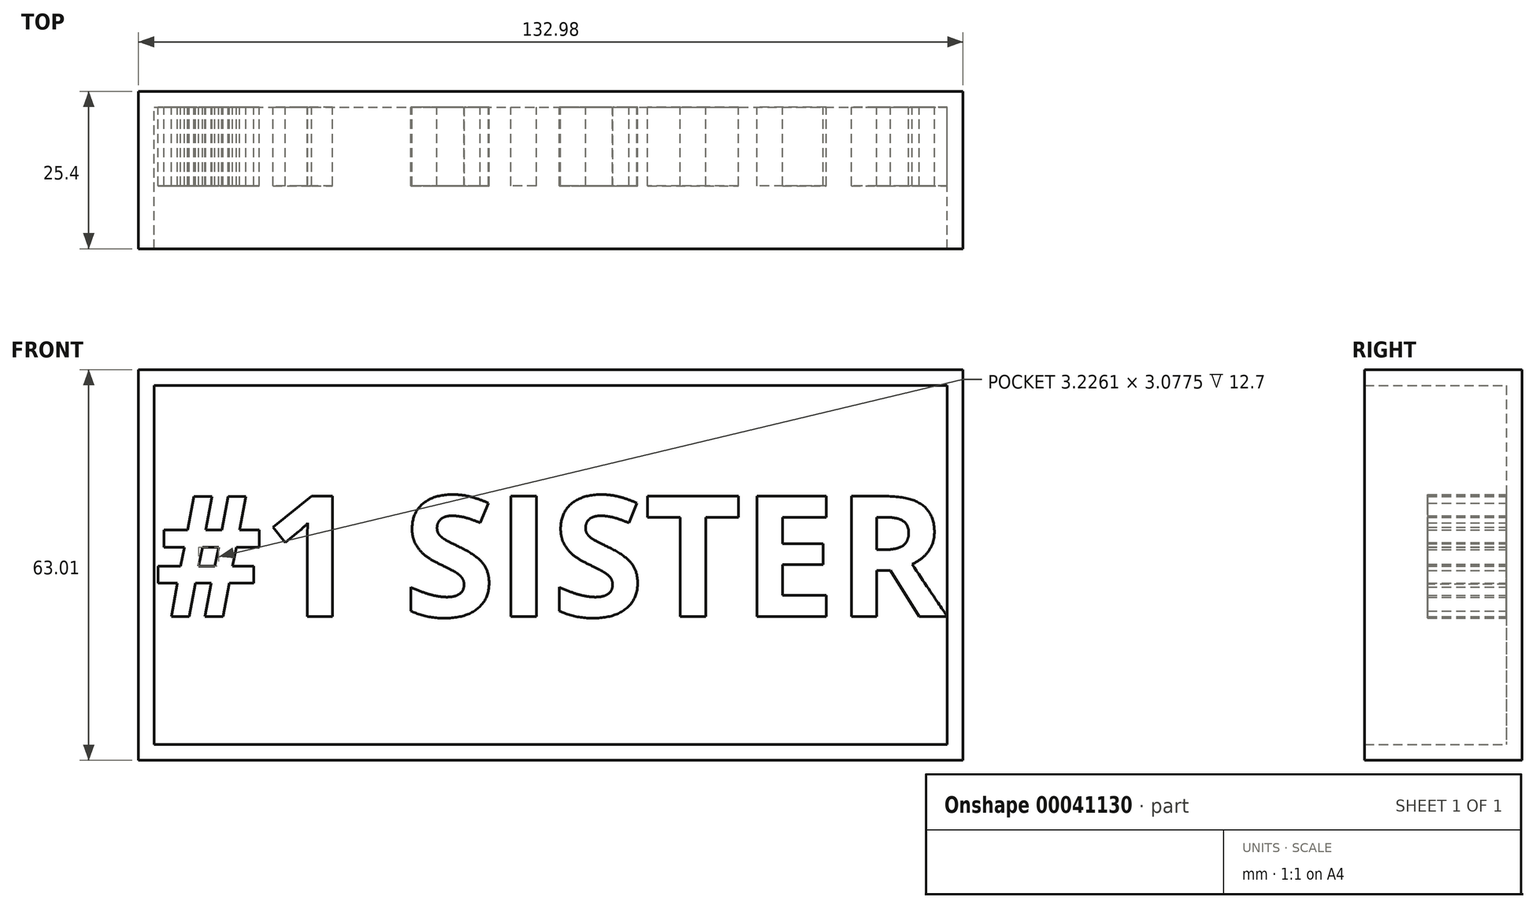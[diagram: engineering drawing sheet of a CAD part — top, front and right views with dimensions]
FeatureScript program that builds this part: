
annotation { "Feature Type Name" : "Feature", "Feature Type Description" : "" }
export const myFeature = defineFeature(function(context is Context, id is Id, definition is map)
    precondition{}
    {
        {
            var Q0;
            Q0=qCreatedBy(makeId("Front.planeOp"),FACE);
            var sketch = newSketch(context, id + "F0", { "sketchPlane" : qUnion([Q0])});
            skLineSegment(sketch, "E0.bottom", {"start": v(-75.97, 55.76) * mm, "end": v(57.01, 55.76) * mm});
            skLineSegment(sketch, "E0.top", {"start": v(-75.97, -7.25) * mm, "end": v(57.01, -7.25) * mm});
            skLineSegment(sketch, "E0.left", {"start": v(-75.97, 55.76) * mm, "end": v(-75.97, -7.25) * mm});
            skLineSegment(sketch, "E0.right", {"start": v(57.01, 55.76) * mm, "end": v(57.01, -7.25) * mm});
            skSolve(sketch);
        }
        {
            var Q0;
            Q0=makeQuery(id+"F0.imprint","IMPRINT",FACE,{"disambiguationData":[TD([[makeQuery(id+"F0.imprint","IMPRINT",EDGE,{"derivedFrom":sQuery(id+"F0.wireOp",EDGE,"E0.bottom")}),-1.0]])]});
            extrude(context, id + "F1", {"entities" : qUnion([Q0]), "depth" : 25.4 * mm});
        }
        {
            var Q0;
            Q0=makeQuery(id+"F1.opExtrude","CAP_FACE",FACE,{"disambiguationData":[OSD([sQuery(id+"F0.wireOp",EDGE,"E0.bottom"),sQuery(id+"F0.wireOp",EDGE,"E0.top"),sQuery(id+"F0.wireOp",EDGE,"E0.left"),sQuery(id+"F0.wireOp",EDGE,"E0.right")])],"isStart":false});
            shell(context, id + "F2", {"entities" : qUnion([Q0]), "thickness" : 2.54 * mm});
        }
        {
            var Q0;
            Q0=makeQuery(id+"F2.opShell","OFFSET_FACE",FACE,{"disambiguationData":[OSD([sQuery(id+"F0.wireOp",EDGE,"E0.bottom"),sQuery(id+"F0.wireOp",EDGE,"E0.top"),sQuery(id+"F0.wireOp",EDGE,"E0.left"),sQuery(id+"F0.wireOp",EDGE,"E0.right")])]});
            var sketch = newSketch(context, id + "F3", { "sketchPlane" : qUnion([Q0])});
            skText(sketch, "E1", { "text": "#1 SISTER", "fontName": "OpenSans-Bold.ttf"});
            const initialGuessF3  = {"E1": [-0.07343, 0.01595, 1, 0, 0.01956]};
            skSetInitialGuess(sketch, initialGuessF3);
            skSolve(sketch);
        }
        {
            var Q0;
            Q0 = qSketchRegion(id + "F3", true);
            extrude(context, id + "F4", {"entities" : qUnion([Q0]), "operationType" : NewBodyOperationType.ADD, "depth" : 12.7 * mm});
        }
    });
